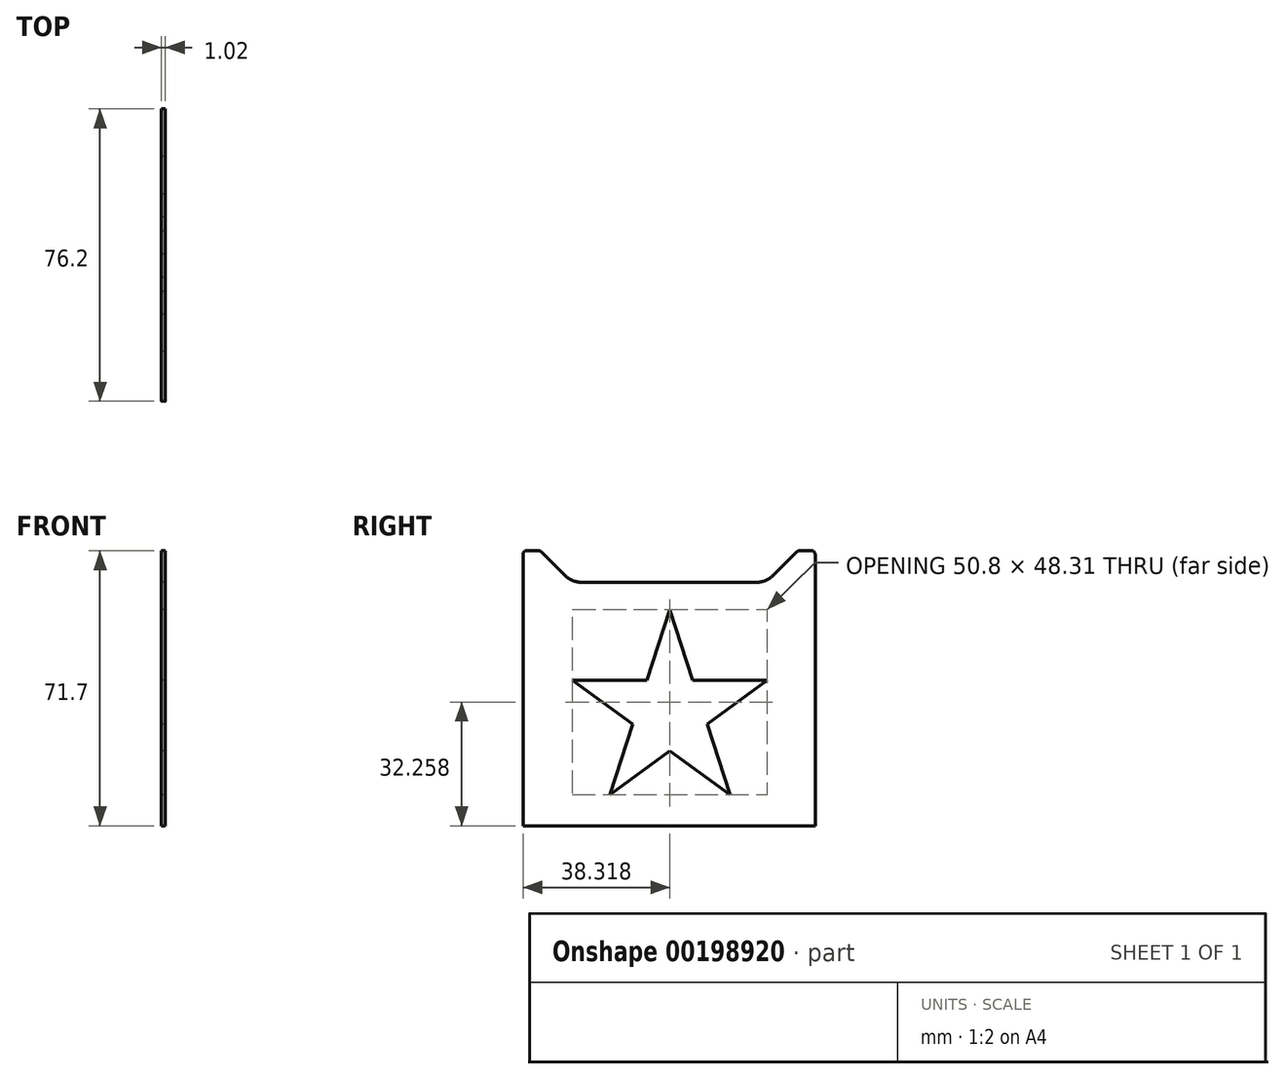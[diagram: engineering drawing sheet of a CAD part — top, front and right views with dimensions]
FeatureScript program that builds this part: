
annotation { "Feature Type Name" : "Feature", "Feature Type Description" : "" }
export const myFeature = defineFeature(function(context is Context, id is Id, definition is map)
    precondition{}
    {
        {
            var Q0;
            Q0=qCreatedBy(makeId("Right.planeOp"),FACE);
            var sketch = newSketch(context, id + "F0", { "sketchPlane" : qUnion([Q0])});
            skLineSegment(sketch, "E0.bottom", {"start": v(0, 0) * mm, "end": v(76.2, 0) * mm});
            skLineSegment(sketch, "E0.left", {"start": v(0, 0) * mm, "end": v(0, 70.81) * mm});
            skLineSegment(sketch, "E0.right", {"start": v(76.2, 0) * mm, "end": v(76.2, 70.81) * mm});
            skLineSegment(sketch, "E1", {"start": v(4.76, 71.44) * mm, "end": v(10.84, 65.36) * mm});
            skLineSegment(sketch, "E2", {"start": v(15.33, 63.5) * mm, "end": v(60.87, 63.5) * mm});
            skLineSegment(sketch, "E3", {"start": v(65.36, 65.36) * mm, "end": v(71.44, 71.44) * mm});
            skLineSegment(sketch, "E4", {"start": v(12.92, 37.96) * mm, "end": v(32.32, 37.96) * mm});
            skLineSegment(sketch, "E5", {"start": v(63.72, 37.96) * mm, "end": v(48.02, 26.55) * mm});
            skLineSegment(sketch, "E6", {"start": v(22.62, 8.1) * mm, "end": v(28.62, 26.55) * mm});
            skLineSegment(sketch, "E7", {"start": v(38.32, 56.41) * mm, "end": v(44.31, 37.96) * mm});
            skLineSegment(sketch, "E8", {"start": v(54.02, 8.1) * mm, "end": v(38.32, 19.5) * mm});
            skLineSegment(sketch, "E9.trimOffspring", {"start": v(28.62, 26.55) * mm, "end": v(12.92, 37.96) * mm});
            skLineSegment(sketch, "E10.trimOffspring", {"start": v(32.32, 37.96) * mm, "end": v(38.32, 56.41) * mm});
            skLineSegment(sketch, "E11.trimOffspring", {"start": v(44.31, 37.96) * mm, "end": v(63.72, 37.96) * mm});
            skLineSegment(sketch, "E12.trimOffspring", {"start": v(48.02, 26.55) * mm, "end": v(54.02, 8.1) * mm});
            skLineSegment(sketch, "E13.trimOffspring", {"start": v(38.32, 19.5) * mm, "end": v(22.62, 8.1) * mm});
            skPoint(sketch, "E14.visualSharp", {"position": v(12.7, 63.5) * mm});
            skArc(sketch, "E14.filletArc", {"start": v(10.84, 65.36) * mm, "mid": v(12.9, 63.98) * mm, "end": v(15.33, 63.5) * mm});
            skPoint(sketch, "E15.visualSharp", {"position": v(63.5, 63.5) * mm});
            skArc(sketch, "E15.filletArc", {"start": v(60.87, 63.5) * mm, "mid": v(63.3, 63.98) * mm, "end": v(65.36, 65.36) * mm});
            skLineSegment(sketch, "E16", {"start": v(0.9, 71.7) * mm, "end": v(4.13, 71.7) * mm});
            skLineSegment(sketch, "E17.trimOffspring", {"start": v(72.07, 71.7) * mm, "end": v(75.3, 71.7) * mm});
            skPoint(sketch, "E18.visualSharp", {"position": v(0, 71.7) * mm});
            skArc(sketch, "E18.filletArc", {"start": v(0.9, 71.7) * mm, "mid": v(0.26, 71.44) * mm, "end": v(0, 70.81) * mm});
            skPoint(sketch, "E19.visualSharp", {"position": v(76.2, 71.7) * mm});
            skArc(sketch, "E19.filletArc", {"start": v(76.2, 70.81) * mm, "mid": v(75.94, 71.44) * mm, "end": v(75.3, 71.7) * mm});
            skPoint(sketch, "E20.visualSharp", {"position": v(71.7, 71.7) * mm});
            skArc(sketch, "E20.filletArc", {"start": v(72.07, 71.7) * mm, "mid": v(71.73, 71.64) * mm, "end": v(71.44, 71.44) * mm});
            skPoint(sketch, "E21.visualSharp", {"position": v(4.5, 71.7) * mm});
            skArc(sketch, "E21.filletArc", {"start": v(4.76, 71.44) * mm, "mid": v(4.47, 71.64) * mm, "end": v(4.13, 71.7) * mm});
            skSolve(sketch);
        }
        {
            var Q0;
            Q0 = qSketchRegion(id + "F0", true);
            extrude(context, id + "F1", {"entities" : qUnion([Q0]), "depth" : 1.02 * mm});
        }
    });
